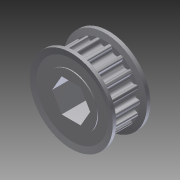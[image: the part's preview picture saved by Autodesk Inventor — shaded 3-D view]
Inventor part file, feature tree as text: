
AUTODESK INVENTOR PART (.ipt)
format: ipt  version: 2014 SP1 (Build 180222100, 222)  size: 651,776 bytes
history: native  units: in
note: dims shown in document units (in); Inventor stores cm internally (conversion verified against a paired STEP export)
features: mirror x1, other x1, imported_body x1
ambient origin geometry x8: Origin, YZ Plane, XZ Plane, XY Plane, X Axis, Y Axis, Z Axis, Center Point
bodies: Body1 (feature_tree)
feature tree (3):
  mirror  "Mirror1"
  other  "217-3225-STEP1"
  imported_body  "Base1"
